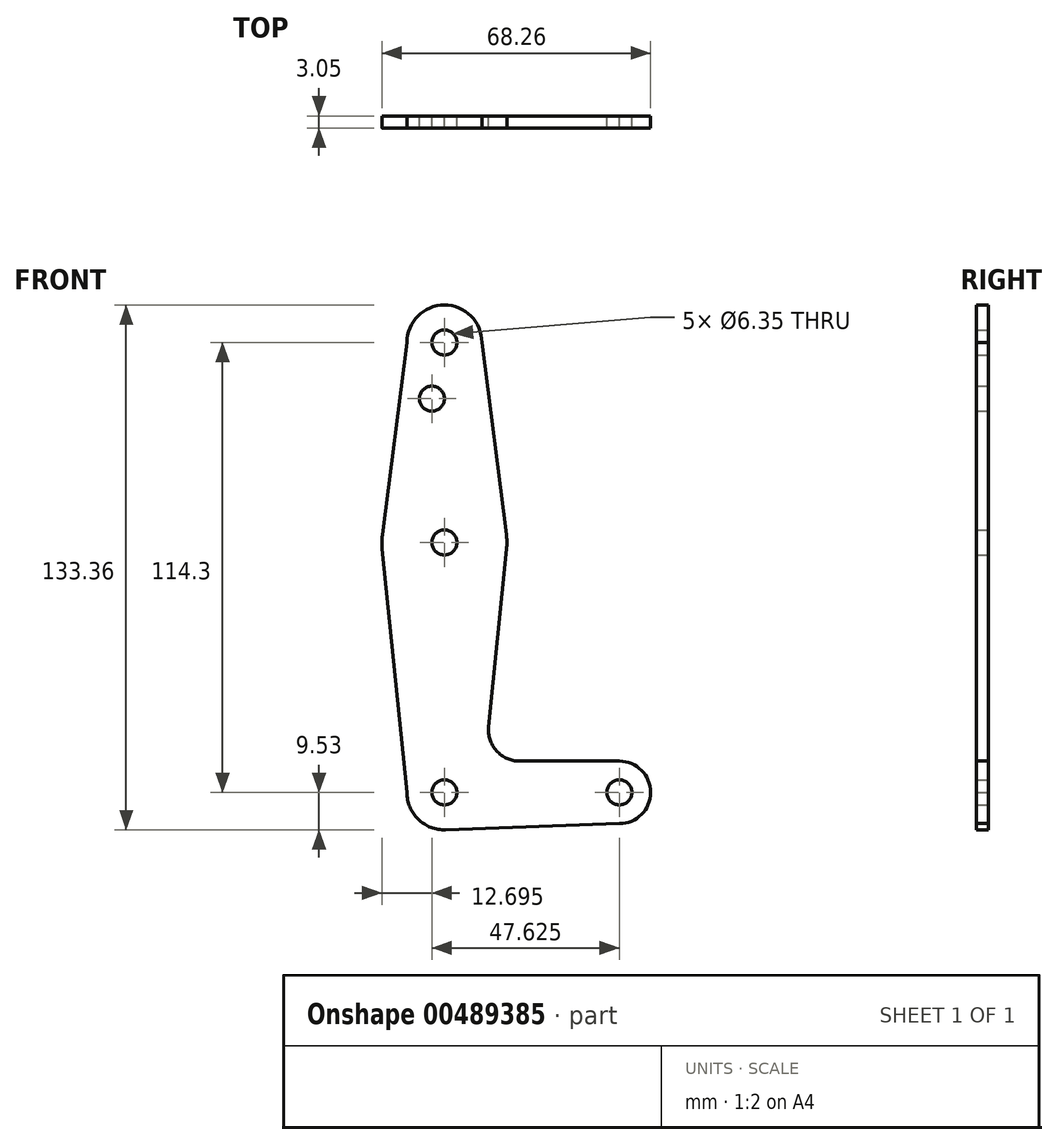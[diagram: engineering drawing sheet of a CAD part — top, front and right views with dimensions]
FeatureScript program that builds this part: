
annotation { "Feature Type Name" : "Feature", "Feature Type Description" : "" }
export const myFeature = defineFeature(function(context is Context, id is Id, definition is map)
    precondition{}
    {
        {
            var Q0;
            Q0=qCreatedBy(makeId("Front.planeOp"),FACE);
            var sketch = newSketch(context, id + "F0", { "sketchPlane" : qUnion([Q0])});
            skCircle(sketch, "E0", {"center": v(0, 0) * mm, "radius": 9.53 * mm});
            skLineSegment(sketch, "E1", {"start": v(0, 0) * mm, "end": v(44.45, 0) * mm, "construction": true});
            skLineSegment(sketch, "E2", {"start": v(0, 0) * mm, "end": v(0, 114.3) * mm, "construction": true});
            skCircle(sketch, "E3", {"center": v(0, 114.3) * mm, "radius": 9.53 * mm});
            skCircle(sketch, "E4", {"center": v(0, 63.5) * mm, "radius": 15.88 * mm});
            skCircle(sketch, "E5", {"center": v(44.45, 0) * mm, "radius": 7.94 * mm});
            skLineSegment(sketch, "E6", {"start": v(9.52, 114.3) * mm, "end": v(15.75, 65.5) * mm});
            skLineSegment(sketch, "E7", {"start": v(-9.53, 114.3) * mm, "end": v(-15.75, 65.5) * mm});
            skLineSegment(sketch, "E8", {"start": v(-9.53, 0) * mm, "end": v(-15.8, 61.9) * mm});
            skLineSegment(sketch, "E9", {"start": v(44.45, -7.94) * mm, "end": v(0, -9.53) * mm});
            skCircle(sketch, "E10", {"center": v(0, 114.3) * mm, "radius": 3.18 * mm});
            skCircle(sketch, "E11", {"center": v(0, 63.5) * mm, "radius": 3.18 * mm});
            skCircle(sketch, "E12", {"center": v(0, 0) * mm, "radius": 3.18 * mm});
            skCircle(sketch, "E13", {"center": v(44.45, 0) * mm, "radius": 3.18 * mm});
            skCircle(sketch, "E14", {"center": v(-3.18, 100.03) * mm, "radius": 3.18 * mm});
            skLineSegment(sketch, "E15", {"start": v(44.45, 7.94) * mm, "end": v(19.12, 7.94) * mm});
            skLineSegment(sketch, "E16", {"start": v(15.8, 61.9) * mm, "end": v(11.22, 16.69) * mm});
            skArc(sketch, "E17.filletArc", {"start": v(11.22, 16.69) * mm, "mid": v(13.23, 10.56) * mm, "end": v(19.12, 7.94) * mm});
            skSolve(sketch);
        }
        {
            var Q0;
            Q0 = qSketchRegion(id + "F0", true);
            extrude(context, id + "F1", {"entities" : qUnion([Q0]), "depth" : 3.05 * mm});
        }
    });
